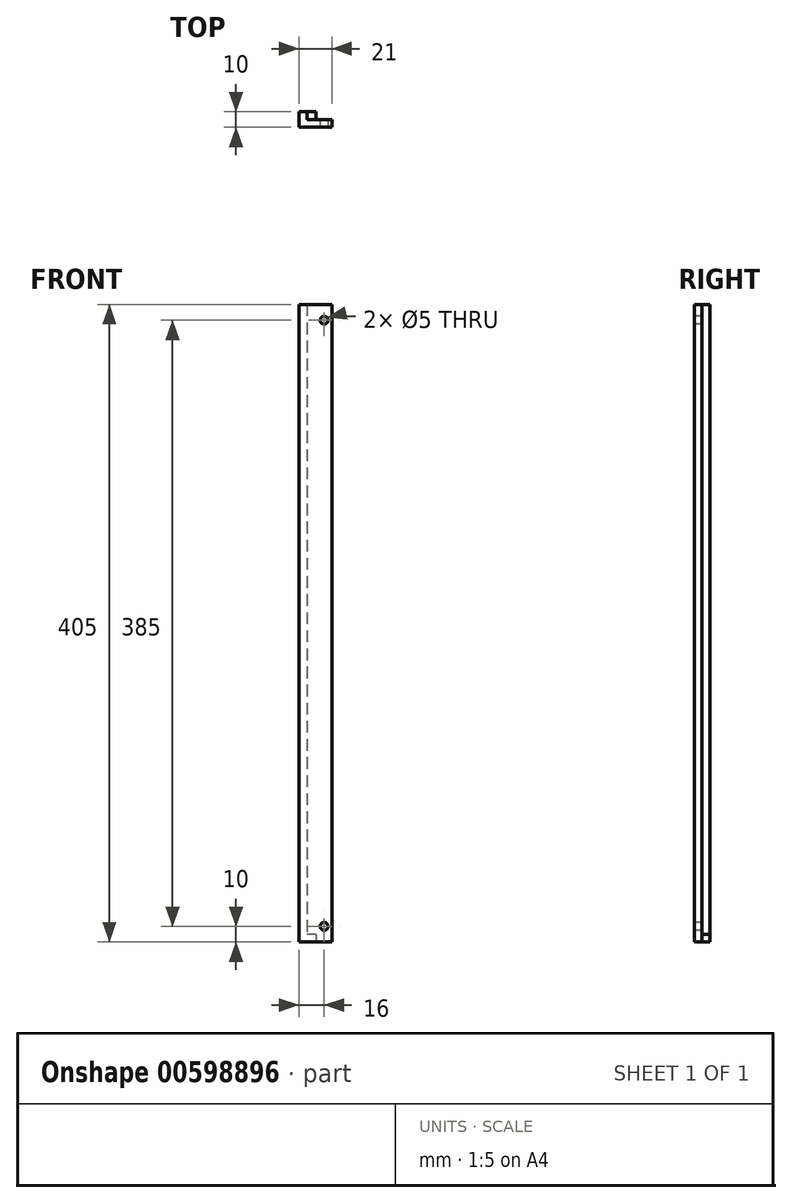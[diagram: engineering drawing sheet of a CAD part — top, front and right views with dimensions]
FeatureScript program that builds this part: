
annotation { "Feature Type Name" : "Feature", "Feature Type Description" : "" }
export const myFeature = defineFeature(function(context is Context, id is Id, definition is map)
    precondition{}
    {
        {
            var Q0;
            Q0=qCreatedBy(makeId("Top.planeOp"),FACE);
            var sketch = newSketch(context, id + "F0", { "sketchPlane" : qUnion([Q0])});
            skLineSegment(sketch, "E0", {"start": v(0, 0) * mm, "end": v(0, -10) * mm});
            skLineSegment(sketch, "E1", {"start": v(0, -10) * mm, "end": v(21, -10) * mm});
            skLineSegment(sketch, "E2", {"start": v(21, -10) * mm, "end": v(21, -5) * mm});
            skLineSegment(sketch, "E3", {"start": v(21, -5) * mm, "end": v(11, -5) * mm});
            skLineSegment(sketch, "E4", {"start": v(11, -5) * mm, "end": v(11, 0) * mm});
            skLineSegment(sketch, "E5", {"start": v(11, 0) * mm, "end": v(6, 0) * mm});
            skLineSegment(sketch, "E6", {"start": v(5, 0) * mm, "end": v(0, 0) * mm});
            skLineSegment(sketch, "E7", {"start": v(5, 0) * mm, "end": v(6, 0) * mm});
            skSolve(sketch);
        }
        {
            var Q0;
            Q0=makeQuery(id+"F0.imprint","IMPRINT",FACE,{"disambiguationData":[TD([[makeQuery(id+"F0.imprint","IMPRINT",EDGE,{"derivedFrom":sQuery(id+"F0.wireOp",EDGE,"E0")}),1.0]])]});
            extrude(context, id + "F1", {"entities" : qUnion([Q0]), "depth" : 5 * mm, "offsetDistance" : 25 * mm});
        }
        {
            var Q0;
            Q0=makeQuery(id+"F1.opExtrude","CAP_FACE",FACE,{"disambiguationData":[OSD([sQuery(id+"F0.wireOp",EDGE,"E0"),sQuery(id+"F0.wireOp",EDGE,"E1"),sQuery(id+"F0.wireOp",EDGE,"E2"),sQuery(id+"F0.wireOp",EDGE,"E3"),sQuery(id+"F0.wireOp",EDGE,"E4"),sQuery(id+"F0.wireOp",EDGE,"E5"),sQuery(id+"F0.wireOp",EDGE,"E6"),sQuery(id+"F0.wireOp",EDGE,"E7")])],"isStart":false});
            var sketch = newSketch(context, id + "F2", { "sketchPlane" : qUnion([Q0])});
            skLineSegment(sketch, "E8", {"start": v(0, 0) * mm, "end": v(0, -10) * mm});
            skLineSegment(sketch, "E9", {"start": v(0, -10) * mm, "end": v(21, -10) * mm});
            skLineSegment(sketch, "E10", {"start": v(21, -10) * mm, "end": v(21, -5) * mm});
            skLineSegment(sketch, "E11", {"start": v(21, -5) * mm, "end": v(11, -5) * mm});
            skLineSegment(sketch, "E12", {"start": v(11, -5) * mm, "end": v(11, 0) * mm});
            skLineSegment(sketch, "E13", {"start": v(11, 0) * mm, "end": v(6, 0) * mm});
            skLineSegment(sketch, "E14", {"start": v(6, 0) * mm, "end": v(6, -5) * mm});
            skLineSegment(sketch, "E15", {"start": v(6, -5) * mm, "end": v(5, -5) * mm});
            skLineSegment(sketch, "E16", {"start": v(5, -5) * mm, "end": v(5, 0) * mm});
            skLineSegment(sketch, "E17", {"start": v(5, 0) * mm, "end": v(0, 0) * mm});
            skSolve(sketch);
        }
        {
            var Q0;
            Q0=makeQuery(id+"F2.imprint","IMPRINT",FACE,{"disambiguationData":[TD([[makeQuery(id+"F2.imprint","IMPRINT",EDGE,{"derivedFrom":sQuery(id+"F2.wireOp",EDGE,"E8")}),1.0]])]});
            extrude(context, id + "F3", {"entities" : qUnion([Q0]), "operationType" : NewBodyOperationType.ADD, "depth" : 400 * mm, "offsetDistance" : 25 * mm});
        }
        {
            var Q0;
            Q0=makeQuery(id+"F3.boolean.opBoolean","MERGE",FACE,{"derivedFrom":[makeQuery(id+"F1.opExtrude","SWEPT_FACE",FACE,{"disambiguationData":[OSD([sQuery(id+"F0.wireOp",EDGE,"E3")])]}),makeQuery(id+"F3.opExtrude","SWEPT_FACE",FACE,{"disambiguationData":[OSD([sQuery(id+"F2.wireOp",EDGE,"E11")])]})]});
            var sketch = newSketch(context, id + "F4", { "sketchPlane" : qUnion([Q0])});
            skLineSegment(sketch, "E18", {"start": v(-16, 0) * mm, "end": v(-16, 10) * mm});
            skSolve(sketch);
        }
        {
            var Q0;
            Q0=sQuery(id+"F4.wireOp",VERTEX,"E18.end");
            var Q1;
            Q1=makeQuery(id+"F1.opExtrude","SWEPT_BODY",BODY,{"disambiguationData":[OSD([sQuery(id+"F0.wireOp",EDGE,"E0"),sQuery(id+"F0.wireOp",EDGE,"E1"),sQuery(id+"F0.wireOp",EDGE,"E2"),sQuery(id+"F0.wireOp",EDGE,"E3"),sQuery(id+"F0.wireOp",EDGE,"E4"),sQuery(id+"F0.wireOp",EDGE,"E5"),sQuery(id+"F0.wireOp",EDGE,"E6"),sQuery(id+"F0.wireOp",EDGE,"E7")])]});
            hole(context, id + "F5", {"style" : HoleStyle.SIMPLE, "endStyle" : HoleEndStyle.THROUGH, "holeDiameter" : 5 * mm, "majorDiameter" : 5 * mm, "isTappedThrough" : true, "tappedDepth" : 12 * mm, "tapClearance" : 3, "locations" : qUnion([Q0]), "scope" : qUnion([Q1])});
        }
        {
            var Q0;
            Q0=makeQuery(id+"F3.boolean.opBoolean","MERGE",FACE,{"derivedFrom":[makeQuery(id+"F1.opExtrude","SWEPT_FACE",FACE,{"disambiguationData":[OSD([sQuery(id+"F0.wireOp",EDGE,"E3")])]}),makeQuery(id+"F3.opExtrude","SWEPT_FACE",FACE,{"disambiguationData":[OSD([sQuery(id+"F2.wireOp",EDGE,"E11")])]})]});
            var sketch = newSketch(context, id + "F6", { "sketchPlane" : qUnion([Q0])});
            skLineSegment(sketch, "E19", {"start": v(-16, 405) * mm, "end": v(-16, 395) * mm});
            skPoint(sketch, "E19.endSnap0", {"position": v(-16, 405) * mm});
            skSolve(sketch);
        }
        {
            var Q0;
            Q0=sQuery(id+"F6.wireOp",VERTEX,"E19.end");
            var Q1;
            Q1=makeQuery(id+"F1.opExtrude","SWEPT_BODY",BODY,{"disambiguationData":[OSD([sQuery(id+"F0.wireOp",EDGE,"E0"),sQuery(id+"F0.wireOp",EDGE,"E1"),sQuery(id+"F0.wireOp",EDGE,"E2"),sQuery(id+"F0.wireOp",EDGE,"E3"),sQuery(id+"F0.wireOp",EDGE,"E4"),sQuery(id+"F0.wireOp",EDGE,"E5"),sQuery(id+"F0.wireOp",EDGE,"E6"),sQuery(id+"F0.wireOp",EDGE,"E7")])]});
            hole(context, id + "F7", {"style" : HoleStyle.SIMPLE, "endStyle" : HoleEndStyle.THROUGH, "holeDiameter" : 5 * mm, "majorDiameter" : 5 * mm, "isTappedThrough" : true, "tappedDepth" : 12 * mm, "tapClearance" : 3, "locations" : qUnion([Q0]), "scope" : qUnion([Q1])});
        }
        {
            var Q0;
            Q0=makeQuery(id+"F3.opExtrude","CAP_FACE",FACE,{"disambiguationData":[OSD([sQuery(id+"F2.wireOp",EDGE,"E8"),sQuery(id+"F2.wireOp",EDGE,"E9"),sQuery(id+"F2.wireOp",EDGE,"E10"),sQuery(id+"F2.wireOp",EDGE,"E11"),sQuery(id+"F2.wireOp",EDGE,"E12"),sQuery(id+"F2.wireOp",EDGE,"E13"),sQuery(id+"F2.wireOp",EDGE,"E14"),sQuery(id+"F2.wireOp",EDGE,"E15"),sQuery(id+"F2.wireOp",EDGE,"E16"),sQuery(id+"F2.wireOp",EDGE,"E17")])],"isStart":false});
            var sketch = newSketch(context, id + "F8", { "sketchPlane" : qUnion([Q0])});
            skLineSegment(sketch, "E20.bottom", {"start": v(6, 0) * mm, "end": v(11, 0) * mm});
            skLineSegment(sketch, "E20.top", {"start": v(6, -5) * mm, "end": v(11, -5) * mm});
            skLineSegment(sketch, "E20.left", {"start": v(6, 0) * mm, "end": v(6, -5) * mm});
            skLineSegment(sketch, "E20.right", {"start": v(11, 0) * mm, "end": v(11, -5) * mm});
            skSolve(sketch);
        }
        {
            var Q0;
            Q0=qSketchRegion(id+"F8",true);
            extrude(context, id + "F9", {"entities" : qUnion([Q0]), "operationType" : NewBodyOperationType.REMOVE, "oppositeDirection" : true, "depth" : 400 * mm, "offsetDistance" : 25 * mm});
        }
    });
